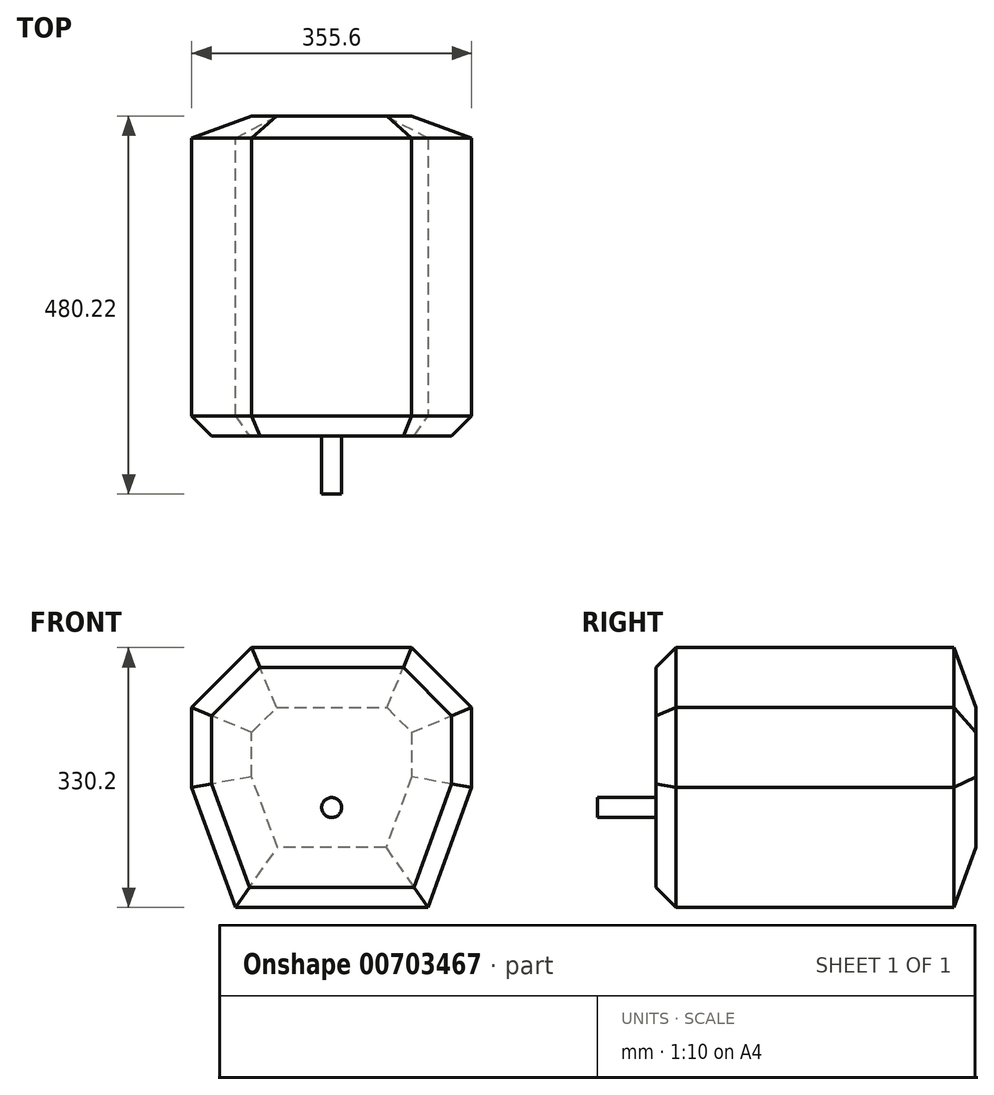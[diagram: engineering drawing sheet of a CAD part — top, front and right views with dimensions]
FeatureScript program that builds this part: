
annotation { "Feature Type Name" : "Feature", "Feature Type Description" : "" }
export const myFeature = defineFeature(function(context is Context, id is Id, definition is map)
    precondition{}
    {
        {
            var Q0;
            Q0=qCreatedBy(makeId("Front.planeOp"),FACE);
            var sketch = newSketch(context, id + "F0", { "sketchPlane" : qUnion([Q0])});
            skLineSegment(sketch, "E0", {"start": v(-203.2, 0) * mm, "end": v(152.4, 0) * mm});
            skLineSegment(sketch, "E1", {"start": v(152.4, 0) * mm, "end": v(152.4, 330.2) * mm});
            skLineSegment(sketch, "E2", {"start": v(152.4, 330.2) * mm, "end": v(-203.2, 330.2) * mm});
            skLineSegment(sketch, "E3", {"start": v(-203.2, 330.2) * mm, "end": v(-203.2, 0) * mm});
            skCircle(sketch, "E4", {"center": v(-25.4, 127) * mm, "radius": 12.7 * mm});
            skSolve(sketch);
        }
        {
            var Q0;
            Q0=makeQuery(id+"F0.imprint","IMPRINT",FACE,{"disambiguationData":[TD([[makeQuery(id+"F0.imprint","IMPRINT",EDGE,{"derivedFrom":sQuery(id+"F0.wireOp",EDGE,"E0")}),1.0]])]});
            var Q1;
            Q1=makeQuery(id+"F0.imprint","IMPRINT",FACE,{"disambiguationData":[TD([[makeQuery(id+"F0.imprint","IMPRINT",EDGE,{"derivedFrom":sQuery(id+"F0.wireOp",EDGE,"E4")}),1.0]])]});
            extrude(context, id + "F1", {"entities" : qUnion([Q0, Q1]), "oppositeDirection" : true, "depth" : 406.4 * mm, "offsetDistance" : 25.4 * mm});
        }
        {
            var Q0;
            Q0=makeQuery(id+"F0.imprint","IMPRINT",FACE,{"disambiguationData":[TD([[makeQuery(id+"F0.imprint","IMPRINT",EDGE,{"derivedFrom":sQuery(id+"F0.wireOp",EDGE,"E4")}),1.0]])]});
            extrude(context, id + "F2", {"entities" : qUnion([Q0]), "operationType" : NewBodyOperationType.ADD, "depth" : 73.82 * mm, "offsetDistance" : 25.4 * mm});
        }
        {
            var Q0;
            Q0=makeQuery(id+"F1.opExtrude","SWEPT_EDGE",EDGE,{"disambiguationData":[OSD([sQuery(id+"F0.wireOp",EDGE,"E2"),sQuery(id+"F0.wireOp",EDGE,"E3")])]});
            var Q1;
            Q1=makeQuery(id+"F1.opExtrude","SWEPT_EDGE",EDGE,{"disambiguationData":[OSD([sQuery(id+"F0.wireOp",EDGE,"E1"),sQuery(id+"F0.wireOp",EDGE,"E2")])]});
            chamfer(context, id + "F3", {"entities" : qUnion([Q0, Q1]), "width" : 76.2 * mm, "tangentPropagation" : true});
        }
        {
            var Q0;
            Q0=makeQuery(id+"F1.opExtrude","SWEPT_EDGE",EDGE,{"disambiguationData":[OSD([sQuery(id+"F0.wireOp",EDGE,"E0"),sQuery(id+"F0.wireOp",EDGE,"E3")])]});
            var Q1;
            Q1=makeQuery(id+"F1.opExtrude","SWEPT_EDGE",EDGE,{"disambiguationData":[OSD([sQuery(id+"F0.wireOp",EDGE,"E0"),sQuery(id+"F0.wireOp",EDGE,"E1")])]});
            chamfer(context, id + "F4", {"entities" : qUnion([Q0, Q1]), "chamferType" : ChamferType.OFFSET_ANGLE, "width" : 152.4 * mm, "oppositeDirection" : false, "angle" : 20 * degree, "tangentPropagation" : true});
        }
        {
            var Q0;
            {var subQ0=sQuery(id+"F0.wireOp",EDGE,"E3");var subQ1=sQuery(id+"F0.wireOp",EDGE,"E2");Q0=makeQuery(id+"F3.opChamfer","BLEND_EDGE",EDGE,{"blendedFrom":[makeQuery(id+"F1.opExtrude","SWEPT_EDGE",EDGE,{"disambiguationData":[OSD([subQ1,subQ0])]}),makeQuery(id+"F1.opExtrude","CAP_FACE",FACE,{"disambiguationData":[OSD([sQuery(id+"F0.wireOp",EDGE,"E0"),sQuery(id+"F0.wireOp",EDGE,"E1"),subQ1,subQ0])],"isStart":true})],"blendedInto":[makeQuery(id+"F1.opExtrude","CAP_FACE",FACE,{"disambiguationData":[OSD([sQuery(id+"F0.wireOp",EDGE,"E0"),sQuery(id+"F0.wireOp",EDGE,"E1"),subQ1,subQ0])],"isStart":true})]});}
            var Q1;
            Q1=makeQuery(id+"F1.opExtrude","CAP_EDGE",EDGE,{"disambiguationData":[OSD([sQuery(id+"F0.wireOp",EDGE,"E3")])],"isStart":true});
            var Q2;
            {var subQ0=sQuery(id+"F0.wireOp",EDGE,"E3");var subQ1=sQuery(id+"F0.wireOp",EDGE,"E0");Q2=makeQuery(id+"F4.opChamfer","BLEND_EDGE",EDGE,{"blendedFrom":[makeQuery(id+"F1.opExtrude","SWEPT_EDGE",EDGE,{"disambiguationData":[OSD([subQ1,subQ0])]}),makeQuery(id+"F1.opExtrude","CAP_FACE",FACE,{"disambiguationData":[OSD([subQ1,sQuery(id+"F0.wireOp",EDGE,"E1"),sQuery(id+"F0.wireOp",EDGE,"E2"),subQ0])],"isStart":true})],"blendedInto":[makeQuery(id+"F1.opExtrude","CAP_FACE",FACE,{"disambiguationData":[OSD([subQ1,sQuery(id+"F0.wireOp",EDGE,"E1"),sQuery(id+"F0.wireOp",EDGE,"E2"),subQ0])],"isStart":true})]});}
            var Q3;
            Q3=makeQuery(id+"F1.opExtrude","CAP_EDGE",EDGE,{"disambiguationData":[OSD([sQuery(id+"F0.wireOp",EDGE,"E0")])],"isStart":true});
            var Q4;
            {var subQ0=sQuery(id+"F0.wireOp",EDGE,"E1");var subQ1=sQuery(id+"F0.wireOp",EDGE,"E0");Q4=makeQuery(id+"F4.opChamfer","BLEND_EDGE",EDGE,{"blendedFrom":[makeQuery(id+"F1.opExtrude","SWEPT_EDGE",EDGE,{"disambiguationData":[OSD([subQ1,subQ0])]}),makeQuery(id+"F1.opExtrude","CAP_FACE",FACE,{"disambiguationData":[OSD([subQ1,subQ0,sQuery(id+"F0.wireOp",EDGE,"E2"),sQuery(id+"F0.wireOp",EDGE,"E3")])],"isStart":true})],"blendedInto":[makeQuery(id+"F1.opExtrude","CAP_FACE",FACE,{"disambiguationData":[OSD([subQ1,subQ0,sQuery(id+"F0.wireOp",EDGE,"E2"),sQuery(id+"F0.wireOp",EDGE,"E3")])],"isStart":true})]});}
            var Q5;
            Q5=makeQuery(id+"F1.opExtrude","CAP_EDGE",EDGE,{"disambiguationData":[OSD([sQuery(id+"F0.wireOp",EDGE,"E1")])],"isStart":true});
            var Q6;
            {var subQ0=sQuery(id+"F0.wireOp",EDGE,"E2");var subQ1=sQuery(id+"F0.wireOp",EDGE,"E1");Q6=makeQuery(id+"F3.opChamfer","BLEND_EDGE",EDGE,{"blendedFrom":[makeQuery(id+"F1.opExtrude","SWEPT_EDGE",EDGE,{"disambiguationData":[OSD([subQ1,subQ0])]}),makeQuery(id+"F1.opExtrude","CAP_FACE",FACE,{"disambiguationData":[OSD([sQuery(id+"F0.wireOp",EDGE,"E0"),subQ1,subQ0,sQuery(id+"F0.wireOp",EDGE,"E3")])],"isStart":true})],"blendedInto":[makeQuery(id+"F1.opExtrude","CAP_FACE",FACE,{"disambiguationData":[OSD([sQuery(id+"F0.wireOp",EDGE,"E0"),subQ1,subQ0,sQuery(id+"F0.wireOp",EDGE,"E3")])],"isStart":true})]});}
            var Q7;
            Q7=makeQuery(id+"F1.opExtrude","CAP_EDGE",EDGE,{"disambiguationData":[OSD([sQuery(id+"F0.wireOp",EDGE,"E2")])],"isStart":true});
            chamfer(context, id + "F5", {"entities" : qUnion([Q0, Q1, Q2, Q3, Q4, Q5, Q6, Q7]), "width" : 25.4 * mm, "tangentPropagation" : true});
        }
        {
            var Q0;
            {var subQ0=sQuery(id+"F0.wireOp",EDGE,"E3");var subQ1=sQuery(id+"F0.wireOp",EDGE,"E0");Q0=makeQuery(id+"F4.opChamfer","BLEND_EDGE",EDGE,{"blendedFrom":[makeQuery(id+"F1.opExtrude","SWEPT_EDGE",EDGE,{"disambiguationData":[OSD([subQ1,subQ0])]}),makeQuery(id+"F1.opExtrude","CAP_FACE",FACE,{"disambiguationData":[OSD([subQ1,sQuery(id+"F0.wireOp",EDGE,"E1"),sQuery(id+"F0.wireOp",EDGE,"E2"),subQ0])],"isStart":false})],"blendedInto":[makeQuery(id+"F1.opExtrude","CAP_FACE",FACE,{"disambiguationData":[OSD([subQ1,sQuery(id+"F0.wireOp",EDGE,"E1"),sQuery(id+"F0.wireOp",EDGE,"E2"),subQ0])],"isStart":false})]});}
            var Q1;
            Q1=makeQuery(id+"F1.opExtrude","CAP_EDGE",EDGE,{"disambiguationData":[OSD([sQuery(id+"F0.wireOp",EDGE,"E3")])],"isStart":false});
            var Q2;
            {var subQ0=sQuery(id+"F0.wireOp",EDGE,"E3");var subQ1=sQuery(id+"F0.wireOp",EDGE,"E2");Q2=makeQuery(id+"F3.opChamfer","BLEND_EDGE",EDGE,{"blendedFrom":[makeQuery(id+"F1.opExtrude","SWEPT_EDGE",EDGE,{"disambiguationData":[OSD([subQ1,subQ0])]}),makeQuery(id+"F1.opExtrude","CAP_FACE",FACE,{"disambiguationData":[OSD([sQuery(id+"F0.wireOp",EDGE,"E0"),sQuery(id+"F0.wireOp",EDGE,"E1"),subQ1,subQ0])],"isStart":false})],"blendedInto":[makeQuery(id+"F1.opExtrude","CAP_FACE",FACE,{"disambiguationData":[OSD([sQuery(id+"F0.wireOp",EDGE,"E0"),sQuery(id+"F0.wireOp",EDGE,"E1"),subQ1,subQ0])],"isStart":false})]});}
            var Q3;
            Q3=makeQuery(id+"F1.opExtrude","CAP_EDGE",EDGE,{"disambiguationData":[OSD([sQuery(id+"F0.wireOp",EDGE,"E2")])],"isStart":false});
            var Q4;
            Q4=makeQuery(id+"F1.opExtrude","CAP_FACE",FACE,{"disambiguationData":[OSD([sQuery(id+"F0.wireOp",EDGE,"E0"),sQuery(id+"F0.wireOp",EDGE,"E1"),sQuery(id+"F0.wireOp",EDGE,"E2"),sQuery(id+"F0.wireOp",EDGE,"E3")])],"isStart":false});
            chamfer(context, id + "F6", {"entities" : qUnion([Q0, Q1, Q2, Q3, Q4]), "chamferType" : ChamferType.OFFSET_ANGLE, "width" : 76.2 * mm, "oppositeDirection" : false, "angle" : 20 * degree, "tangentPropagation" : true});
        }
    });
